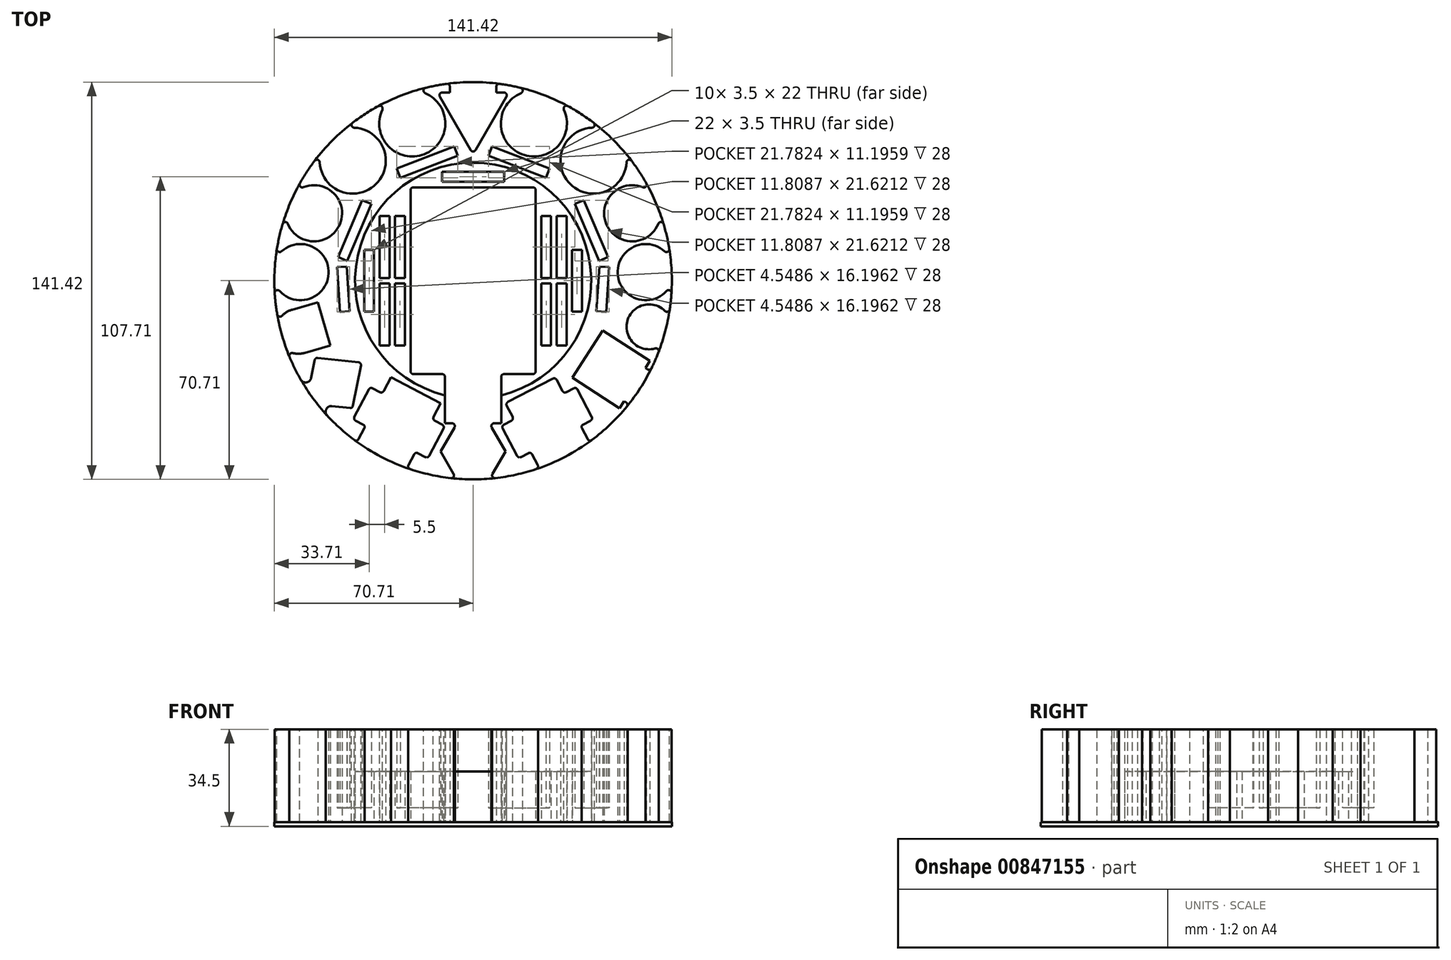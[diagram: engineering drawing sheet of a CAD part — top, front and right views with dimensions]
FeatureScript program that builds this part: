
annotation { "Feature Type Name" : "Feature", "Feature Type Description" : "" }
export const myFeature = defineFeature(function(context is Context, id is Id, definition is map)
    precondition{}
    {
        {
            var Q0;
            Q0=qCreatedBy(makeId("Top.planeOp"),FACE);
            var sketch = newSketch(context, id + "F0", { "sketchPlane" : qUnion([Q0])});
            skLineSegment(sketch, "E0.bottom", {"start": v(-22.25, 33.25) * mm, "end": v(22.25, 33.25) * mm});
            skLineSegment(sketch, "E0.top", {"start": v(-22.25, -33.25) * mm, "end": v(22.25, -33.25) * mm});
            skLineSegment(sketch, "E0.left", {"start": v(-22.25, 33.25) * mm, "end": v(-22.25, -33.25) * mm});
            skLineSegment(sketch, "E0.right", {"start": v(22.25, 33.25) * mm, "end": v(22.25, -33.25) * mm});
            skPoint(sketch, "E0.middle", {"position": v(0, 0) * mm});
            skCircle(sketch, "E1", {"center": v(0, 0) * mm, "radius": 42 * mm});
            skCircle(sketch, "E2", {"center": v(0, 0) * mm, "radius": 70.71 * mm});
            skPoint(sketch, "E3.middle", {"position": v(0, 57) * mm});
            skLineSegment(sketch, "E4.bottom", {"start": v(-10, -33.25) * mm, "end": v(10, -33.25) * mm});
            skLineSegment(sketch, "E4.top", {"start": v(-10, -50.75) * mm, "end": v(10, -50.75) * mm});
            skLineSegment(sketch, "E4.left", {"start": v(-10, -33.25) * mm, "end": v(-10, -50.75) * mm});
            skLineSegment(sketch, "E4.right", {"start": v(10, -33.25) * mm, "end": v(10, -50.75) * mm});
            skPoint(sketch, "E4.middle", {"position": v(0, -42) * mm});
            skCircle(sketch, "E5", {"center": v(0, 0) * mm, "radius": 60 * mm, "construction": true});
            skCircle(sketch, "E6", {"center": v(21.63, 55.97) * mm, "radius": 11.75 * mm});
            skCircle(sketch, "E7", {"center": v(0, 0) * mm, "radius": 61.5 * mm, "construction": true});
            skCircle(sketch, "E8", {"center": v(56.62, 24) * mm, "radius": 10 * mm});
            skCircle(sketch, "E9", {"center": v(0, 0) * mm, "radius": 60.5 * mm, "construction": true});
            skCircle(sketch, "E10", {"center": v(42.84, 42.72) * mm, "radius": 11.75 * mm});
            skCircle(sketch, "E11", {"center": v(61.42, 3.05) * mm, "radius": 10 * mm});
            skCircle(sketch, "E12", {"center": v(0, 0) * mm, "radius": 74 * mm, "construction": true});
            skCircle(sketch, "E13", {"center": v(0, 0) * mm, "radius": 59 * mm, "construction": true});
            skCircle(sketch, "E14.MirrorC", {"center": v(-21.63, 55.97) * mm, "radius": 11.75 * mm});
            skCircle(sketch, "E15.MirrorC", {"center": v(-42.84, 42.72) * mm, "radius": 11.75 * mm});
            skCircle(sketch, "E16.MirrorC", {"center": v(-56.62, 24) * mm, "radius": 10 * mm});
            skCircle(sketch, "E17.MirrorC", {"center": v(-61.42, 3.05) * mm, "radius": 10 * mm});
            skLineSegment(sketch, "E18.bottom", {"start": v(-16.1, -63.23) * mm, "end": v(-42.69, -49.35) * mm});
            skLineSegment(sketch, "E18.top", {"start": v(-10.08, -51.7) * mm, "end": v(-36.67, -37.82) * mm});
            skLineSegment(sketch, "E18.left", {"start": v(-16.1, -63.23) * mm, "end": v(-10.08, -51.7) * mm});
            skLineSegment(sketch, "E18.right", {"start": v(-42.69, -49.35) * mm, "end": v(-36.67, -37.82) * mm});
            skPoint(sketch, "E18.middle", {"position": v(-26.38, -50.53) * mm});
            skLineSegment(sketch, "E19.bottom", {"start": v(-11.5, -43.63) * mm, "end": v(-29.23, -34.38) * mm});
            skLineSegment(sketch, "E19.top", {"start": v(-23.53, -66.68) * mm, "end": v(-41.26, -57.42) * mm});
            skLineSegment(sketch, "E19.left", {"start": v(-11.5, -43.63) * mm, "end": v(-23.53, -66.68) * mm});
            skLineSegment(sketch, "E19.right", {"start": v(-29.23, -34.38) * mm, "end": v(-41.26, -57.42) * mm});
            skLineSegment(sketch, "E20.MirrorCS", {"start": v(11.5, -43.63) * mm, "end": v(29.23, -34.38) * mm});
            skLineSegment(sketch, "E21.MirrorCS", {"start": v(10.08, -51.7) * mm, "end": v(36.67, -37.82) * mm});
            skLineSegment(sketch, "E22.MirrorCS", {"start": v(29.23, -34.38) * mm, "end": v(41.26, -57.42) * mm});
            skLineSegment(sketch, "E23.MirrorCS", {"start": v(42.69, -49.35) * mm, "end": v(36.67, -37.82) * mm});
            skLineSegment(sketch, "E24.MirrorCS", {"start": v(16.1, -63.23) * mm, "end": v(10.08, -51.7) * mm});
            skLineSegment(sketch, "E25.MirrorCS", {"start": v(11.5, -43.63) * mm, "end": v(23.53, -66.68) * mm});
            skLineSegment(sketch, "E26.MirrorCS", {"start": v(23.53, -66.68) * mm, "end": v(41.26, -57.42) * mm});
            skLineSegment(sketch, "E27.MirrorCS", {"start": v(16.1, -63.23) * mm, "end": v(42.69, -49.35) * mm});
            skLineSegment(sketch, "E28", {"start": v(-24.25, 29.08) * mm, "end": v(-24.25, -29.92) * mm, "construction": true});
            skCircle(sketch, "E29", {"center": v(0, 0) * mm, "radius": 40 * mm, "construction": true});
            skLineSegment(sketch, "E30", {"start": v(-46.76, 1) * mm, "end": v(-10.29, 1) * mm, "construction": true});
            skLineSegment(sketch, "E31.bottom", {"start": v(-24.25, 1) * mm, "end": v(-27.75, 1) * mm});
            skLineSegment(sketch, "E31.top", {"start": v(-24.25, 23) * mm, "end": v(-27.75, 23) * mm});
            skLineSegment(sketch, "E31.left", {"start": v(-24.25, 1) * mm, "end": v(-24.25, 23) * mm});
            skLineSegment(sketch, "E31.right", {"start": v(-27.75, 1) * mm, "end": v(-27.75, 23) * mm});
            skLineSegment(sketch, "E32.bottom", {"start": v(-29.75, 1) * mm, "end": v(-33.25, 1) * mm});
            skLineSegment(sketch, "E32.top", {"start": v(-29.75, 23) * mm, "end": v(-33.25, 23) * mm});
            skLineSegment(sketch, "E32.left", {"start": v(-29.75, 1) * mm, "end": v(-29.75, 23) * mm});
            skLineSegment(sketch, "E32.right", {"start": v(-33.25, 1) * mm, "end": v(-33.25, 23) * mm});
            skLineSegment(sketch, "E33.bottom", {"start": v(-35.25, 11) * mm, "end": v(-38.75, 11) * mm});
            skLineSegment(sketch, "E33.top", {"start": v(-35.25, -11) * mm, "end": v(-38.75, -11) * mm});
            skLineSegment(sketch, "E33.left", {"start": v(-35.25, 11) * mm, "end": v(-35.25, -11) * mm});
            skLineSegment(sketch, "E33.right", {"start": v(-38.75, 11) * mm, "end": v(-38.75, -11) * mm});
            skPoint(sketch, "E33.middle", {"position": v(-37, 0) * mm});
            skLineSegment(sketch, "E34.MirrorCS", {"start": v(-29.75, -1) * mm, "end": v(-29.75, -23) * mm});
            skLineSegment(sketch, "E35.MirrorCS", {"start": v(-27.75, -1) * mm, "end": v(-27.75, -23) * mm});
            skLineSegment(sketch, "E36.MirrorCS", {"start": v(-29.75, -1) * mm, "end": v(-33.25, -1) * mm});
            skLineSegment(sketch, "E37.MirrorCS", {"start": v(-24.25, -1) * mm, "end": v(-27.75, -1) * mm});
            skLineSegment(sketch, "E38.MirrorCS", {"start": v(-24.25, -23) * mm, "end": v(-27.75, -23) * mm});
            skLineSegment(sketch, "E39.MirrorCS", {"start": v(-29.75, -23) * mm, "end": v(-33.25, -23) * mm});
            skLineSegment(sketch, "E40.MirrorCS", {"start": v(-33.25, -1) * mm, "end": v(-33.25, -23) * mm});
            skLineSegment(sketch, "E41.MirrorCS", {"start": v(-24.25, -1) * mm, "end": v(-24.25, -23) * mm});
            skLineSegment(sketch, "E42.MirrorCS", {"start": v(24.25, -1) * mm, "end": v(24.25, -23) * mm});
            skLineSegment(sketch, "E43.MirrorCS", {"start": v(24.25, 1) * mm, "end": v(24.25, 23) * mm});
            skLineSegment(sketch, "E44.MirrorCS", {"start": v(29.75, 1) * mm, "end": v(33.25, 1) * mm});
            skLineSegment(sketch, "E45.MirrorCS", {"start": v(29.75, -1) * mm, "end": v(33.25, -1) * mm});
            skLineSegment(sketch, "E46.MirrorCS", {"start": v(24.25, 1) * mm, "end": v(27.75, 1) * mm});
            skLineSegment(sketch, "E47.MirrorCS", {"start": v(24.25, -1) * mm, "end": v(27.75, -1) * mm});
            skLineSegment(sketch, "E48.MirrorCS", {"start": v(24.25, 29.08) * mm, "end": v(24.25, -29.92) * mm, "construction": true});
            skLineSegment(sketch, "E49.MirrorCS", {"start": v(24.25, -23) * mm, "end": v(27.75, -23) * mm});
            skLineSegment(sketch, "E50.MirrorCS", {"start": v(35.25, 11) * mm, "end": v(38.75, 11) * mm});
            skLineSegment(sketch, "E51.MirrorCS", {"start": v(29.75, -1) * mm, "end": v(29.75, -23) * mm});
            skLineSegment(sketch, "E52.MirrorCS", {"start": v(35.25, -11) * mm, "end": v(38.75, -11) * mm});
            skLineSegment(sketch, "E53.MirrorCS", {"start": v(29.75, 23) * mm, "end": v(33.25, 23) * mm});
            skLineSegment(sketch, "E54.MirrorCS", {"start": v(38.75, 11) * mm, "end": v(38.75, -11) * mm});
            skLineSegment(sketch, "E55.MirrorCS", {"start": v(24.25, 23) * mm, "end": v(27.75, 23) * mm});
            skPoint(sketch, "E56.MirrorP", {"position": v(37, 0) * mm});
            skLineSegment(sketch, "E57.MirrorCS", {"start": v(46.76, 1) * mm, "end": v(10.29, 1) * mm, "construction": true});
            skLineSegment(sketch, "E58.MirrorCS", {"start": v(27.75, -1) * mm, "end": v(27.75, -23) * mm});
            skLineSegment(sketch, "E59.MirrorCS", {"start": v(33.25, 1) * mm, "end": v(33.25, 23) * mm});
            skLineSegment(sketch, "E60.MirrorCS", {"start": v(35.25, 11) * mm, "end": v(35.25, -11) * mm});
            skLineSegment(sketch, "E61.MirrorCS", {"start": v(29.75, -23) * mm, "end": v(33.25, -23) * mm});
            skLineSegment(sketch, "E62.MirrorCS", {"start": v(29.75, 1) * mm, "end": v(29.75, 23) * mm});
            skLineSegment(sketch, "E63.MirrorCS", {"start": v(27.75, 1) * mm, "end": v(27.75, 23) * mm});
            skLineSegment(sketch, "E64.MirrorCS", {"start": v(33.25, -1) * mm, "end": v(33.25, -23) * mm});
            skLineSegment(sketch, "E65.bottom", {"start": v(11, 35.25) * mm, "end": v(-11, 35.25) * mm});
            skLineSegment(sketch, "E65.top", {"start": v(11, 38.75) * mm, "end": v(-11, 38.75) * mm});
            skLineSegment(sketch, "E65.left", {"start": v(11, 35.25) * mm, "end": v(11, 38.75) * mm});
            skLineSegment(sketch, "E65.right", {"start": v(-11, 35.25) * mm, "end": v(-11, 38.75) * mm});
            skPoint(sketch, "E65.middle", {"position": v(0, 37) * mm});
            skLineSegment(sketch, "E66", {"start": v(0, 0) * mm, "end": v(-21.63, 55.97) * mm, "construction": true});
            skLineSegment(sketch, "E67.bottom", {"start": v(-6.68, 47.8) * mm, "end": v(-27.2, 39.87) * mm});
            skLineSegment(sketch, "E67.top", {"start": v(-5.42, 44.54) * mm, "end": v(-25.94, 36.6) * mm});
            skLineSegment(sketch, "E67.left", {"start": v(-6.68, 47.8) * mm, "end": v(-5.42, 44.54) * mm});
            skLineSegment(sketch, "E67.right", {"start": v(-27.2, 39.87) * mm, "end": v(-25.94, 36.6) * mm});
            skPoint(sketch, "E67.middle", {"position": v(-16.31, 42.2) * mm});
            skLineSegment(sketch, "E68", {"start": v(-56.62, 24) * mm, "end": v(0, 0) * mm, "construction": true});
            skLineSegment(sketch, "E69.bottom", {"start": v(-36.22, 27.3) * mm, "end": v(-39.44, 28.67) * mm});
            skLineSegment(sketch, "E69.top", {"start": v(-44.8, 7.04) * mm, "end": v(-48.03, 8.41) * mm});
            skLineSegment(sketch, "E69.left", {"start": v(-36.22, 27.3) * mm, "end": v(-44.8, 7.04) * mm});
            skLineSegment(sketch, "E69.right", {"start": v(-39.44, 28.67) * mm, "end": v(-48.03, 8.41) * mm});
            skPoint(sketch, "E69.middle", {"position": v(-42.12, 17.86) * mm});
            skLineSegment(sketch, "E70.MirrorCS", {"start": v(27.2, 39.87) * mm, "end": v(25.94, 36.6) * mm});
            skLineSegment(sketch, "E71.MirrorCS", {"start": v(6.68, 47.8) * mm, "end": v(27.2, 39.87) * mm});
            skLineSegment(sketch, "E72.MirrorCS", {"start": v(5.42, 44.54) * mm, "end": v(25.94, 36.6) * mm});
            skLineSegment(sketch, "E73.MirrorCS", {"start": v(6.68, 47.8) * mm, "end": v(5.42, 44.54) * mm});
            skLineSegment(sketch, "E74.MirrorCS", {"start": v(39.44, 28.67) * mm, "end": v(48.03, 8.41) * mm});
            skLineSegment(sketch, "E75.MirrorCS", {"start": v(36.22, 27.3) * mm, "end": v(44.8, 7.04) * mm});
            skLineSegment(sketch, "E76.MirrorCS", {"start": v(36.22, 27.3) * mm, "end": v(39.44, 28.67) * mm});
            skLineSegment(sketch, "E77.MirrorCS", {"start": v(44.8, 7.04) * mm, "end": v(48.03, 8.41) * mm});
            skLineSegment(sketch, "E78", {"start": v(0, 0) * mm, "end": v(-52.23, -3.46) * mm, "construction": true});
            skLineSegment(sketch, "E79.bottom", {"start": v(-48.42, 4.81) * mm, "end": v(-44.93, 5.04) * mm});
            skLineSegment(sketch, "E79.top", {"start": v(-47.37, -11.15) * mm, "end": v(-43.87, -10.92) * mm});
            skLineSegment(sketch, "E79.left", {"start": v(-48.42, 4.81) * mm, "end": v(-47.37, -11.15) * mm});
            skLineSegment(sketch, "E79.right", {"start": v(-44.93, 5.04) * mm, "end": v(-43.87, -10.92) * mm});
            skPoint(sketch, "E79.middle", {"position": v(-46.15, -3.05) * mm});
            skLineSegment(sketch, "E80.MirrorCS", {"start": v(48.42, 4.81) * mm, "end": v(44.93, 5.04) * mm});
            skLineSegment(sketch, "E81.MirrorCS", {"start": v(47.37, -11.15) * mm, "end": v(43.87, -10.92) * mm});
            skLineSegment(sketch, "E82.MirrorCS", {"start": v(48.42, 4.81) * mm, "end": v(47.37, -11.15) * mm});
            skLineSegment(sketch, "E83.MirrorCS", {"start": v(44.93, 5.04) * mm, "end": v(43.87, -10.92) * mm});
            skPoint(sketch, "E84.MirrorP", {"position": v(46.15, -3.05) * mm});
            skCircle(sketch, "E85.cCircle", {"center": v(0, -60.75) * mm, "radius": 10 * mm, "construction": true});
            skLineSegment(sketch, "E85.0", {"start": v(-5.77, -50.75) * mm, "end": v(5.77, -50.75) * mm});
            skLineSegment(sketch, "E85.1", {"start": v(5.77, -50.75) * mm, "end": v(11.55, -60.75) * mm});
            skLineSegment(sketch, "E85.2", {"start": v(11.55, -60.75) * mm, "end": v(5.77, -70.75) * mm});
            skLineSegment(sketch, "E85.3", {"start": v(5.77, -70.75) * mm, "end": v(-5.77, -70.75) * mm});
            skLineSegment(sketch, "E85.4", {"start": v(-5.77, -70.75) * mm, "end": v(-11.55, -60.75) * mm});
            skLineSegment(sketch, "E85.5", {"start": v(-11.55, -60.75) * mm, "end": v(-5.77, -50.75) * mm});
            skPoint(sketch, "E85.0.midPoint", {"position": v(0, -50.75) * mm});
            skLineSegment(sketch, "E86.MirrorCS", {"start": v(-13.28, 68) * mm, "end": v(13.28, 68) * mm});
            skLineSegment(sketch, "E87", {"start": v(13.28, 68) * mm, "end": v(0, 45) * mm});
            skLineSegment(sketch, "E88", {"start": v(0, 45) * mm, "end": v(-13.28, 68) * mm});
            skLineSegment(sketch, "E89", {"start": v(-8.28, 70.22) * mm, "end": v(-8.28, 68) * mm});
            skLineSegment(sketch, "E90.MirrorCS", {"start": v(8.28, 70.22) * mm, "end": v(8.28, 68) * mm});
            skCircle(sketch, "E91", {"center": v(-62.16, -17.99) * mm, "radius": 8 * mm});
            skLineSegment(sketch, "E92", {"start": v(-59.94, -25.67) * mm, "end": v(-50.81, -23.03) * mm});
            skLineSegment(sketch, "E93", {"start": v(-50.81, -23.03) * mm, "end": v(-55.26, -7.66) * mm});
            skLineSegment(sketch, "E94", {"start": v(-55.26, -7.66) * mm, "end": v(-64.38, -10.3) * mm});
            skLineSegment(sketch, "E95.bottom", {"start": v(62.92, -28.54) * mm, "end": v(46.1, -17.73) * mm});
            skLineSegment(sketch, "E95.top", {"start": v(52.1, -45.37) * mm, "end": v(35.28, -34.56) * mm});
            skLineSegment(sketch, "E95.left", {"start": v(62.92, -28.54) * mm, "end": v(52.1, -45.37) * mm});
            skLineSegment(sketch, "E95.right", {"start": v(46.1, -17.73) * mm, "end": v(35.28, -34.56) * mm});
            skPoint(sketch, "E95.middle", {"position": v(49.1, -31.55) * mm});
            skLineSegment(sketch, "E96", {"start": v(49.1, -31.55) * mm, "end": v(0, 0) * mm, "construction": true});
            skLineSegment(sketch, "E97", {"start": v(61.3, -31.06) * mm, "end": v(62.98, -32.14) * mm});
            skLineSegment(sketch, "E98.MirrorCS", {"start": v(53.73, -42.84) * mm, "end": v(55.41, -43.92) * mm});
            skLineSegment(sketch, "E99", {"start": v(-59.4, -43.66) * mm, "end": v(-56.19, -27.37) * mm});
            skLineSegment(sketch, "E100", {"start": v(-56.19, -27.37) * mm, "end": v(-39.68, -29.16) * mm});
            skLineSegment(sketch, "E101", {"start": v(-39.68, -29.16) * mm, "end": v(-42.9, -45.45) * mm});
            skLineSegment(sketch, "E102", {"start": v(-42.9, -45.45) * mm, "end": v(-59.4, -43.66) * mm});
            skCircle(sketch, "E103", {"center": v(0, 0) * mm, "radius": 62.5 * mm, "construction": true});
            skLineSegment(sketch, "E104", {"start": v(-69.25, -14.29) * mm, "end": v(-66.18, -24.9) * mm, "construction": true});
            skCircle(sketch, "E105.MirrorC", {"center": v(62.6, -16.42) * mm, "radius": 8 * mm});
            skLineSegment(sketch, "E106", {"start": v(-12.7, 67) * mm, "end": v(12.7, 67) * mm});
            skLineSegment(sketch, "E107", {"start": v(-8.28, 68) * mm, "end": v(-8.28, 67) * mm});
            skLineSegment(sketch, "E108", {"start": v(8.28, 68) * mm, "end": v(8.28, 67) * mm});
            skLineSegment(sketch, "E109.bottom", {"start": v(28.25, 38.25) * mm, "end": v(-28.25, 38.25) * mm, "construction": true});
            skLineSegment(sketch, "E109.top", {"start": v(28.25, -38.25) * mm, "end": v(-28.25, -38.25) * mm, "construction": true});
            skLineSegment(sketch, "E109.left", {"start": v(28.25, 38.25) * mm, "end": v(28.25, -38.25) * mm, "construction": true});
            skLineSegment(sketch, "E109.right", {"start": v(-28.25, 38.25) * mm, "end": v(-28.25, -38.25) * mm, "construction": true});
            skSolve(sketch);
        }
        {
            var Q0;
            Q0=makeQuery(id+"F0.imprint","IMPRINT",FACE,{"disambiguationData":[TD([[makeQuery(id+"F0.imprint","IMPRINT",EDGE,{"derivedFrom":sQuery(id+"F0.wireOp",EDGE,"E0.bottom")}),1.0]])]});
            extrude(context, id + "F1", {"entities" : qUnion([Q0]), "depth" : 18 * mm, "offsetDistance" : 25 * mm});
        }
        {
            var Q0;
            Q0=makeQuery(id+"F1.opExtrude","SWEPT_EDGE",EDGE,{"disambiguationData":[OSD([sQuery(id+"F0.wireOp",EDGE,"E0.bottom"),sQuery(id+"F0.wireOp",EDGE,"E0.left")])]});
            var Q1;
            Q1=makeQuery(id+"F1.opExtrude","SWEPT_EDGE",EDGE,{"disambiguationData":[OSD([sQuery(id+"F0.wireOp",EDGE,"E0.bottom"),sQuery(id+"F0.wireOp",EDGE,"E0.right")])]});
            var Q2;
            Q2=makeQuery(id+"F1.opExtrude","SWEPT_EDGE",EDGE,{"disambiguationData":[OSD([sQuery(id+"F0.wireOp",EDGE,"E0.top"),sQuery(id+"F0.wireOp",EDGE,"E0.left")])]});
            var Q3;
            Q3=makeQuery(id+"F1.opExtrude","SWEPT_EDGE",EDGE,{"disambiguationData":[OSD([sQuery(id+"F0.wireOp",EDGE,"E0.top"),sQuery(id+"F0.wireOp",EDGE,"E4.bottom"),sQuery(id+"F0.wireOp",EDGE,"E4.left")])]});
            var Q4;
            Q4=makeQuery(id+"F1.opExtrude","SWEPT_EDGE",EDGE,{"disambiguationData":[OSD([sQuery(id+"F0.wireOp",EDGE,"E0.top"),sQuery(id+"F0.wireOp",EDGE,"E4.bottom"),sQuery(id+"F0.wireOp",EDGE,"E4.right")])]});
            var Q5;
            Q5=makeQuery(id+"F1.opExtrude","SWEPT_EDGE",EDGE,{"disambiguationData":[OSD([sQuery(id+"F0.wireOp",EDGE,"E0.top"),sQuery(id+"F0.wireOp",EDGE,"E0.right")])]});
            fillet(context, id + "F2", {"entities" : qUnion([Q0, Q1, Q2, Q3, Q4, Q5]), "radius" : 1 * mm, "tangentPropagation" : true, "allowEdgeOverflow" : false});
        }
        {
            var Q0;
            {var subQ69=sQuery(id+"F0.wireOp",EDGE,"E4.top");Q0=makeQuery(id+"F0.imprint","IMPRINT",FACE,{"disambiguationData":[TD([[makeQuery(id+"F0.imprint","IMPRINT",EDGE,{"derivedFrom":subQ69}),-1.0]])]});}
            var Q1;
            {var subQ3=sQuery(id+"F0.wireOp",EDGE,"E107");Q1=makeQuery(id+"F0.imprint","IMPRINT",FACE,{"disambiguationData":[TD([[makeQuery(id+"F0.imprint","IMPRINT",EDGE,{"derivedFrom":subQ3}),-1.0]])]});}
            var Q2;
            {var subQ3=sQuery(id+"F0.wireOp",EDGE,"E108");Q2=makeQuery(id+"F0.imprint","IMPRINT",FACE,{"disambiguationData":[TD([[makeQuery(id+"F0.imprint","IMPRINT",EDGE,{"derivedFrom":subQ3}),1.0]])]});}
            extrude(context, id + "F3", {"entities" : qUnion([Q0, Q1, Q2]), "depth" : 33 * mm, "offsetDistance" : 25 * mm});
        }
        {
            var Q0;
            Q0=makeQuery(id+"F3.opExtrude","SWEPT_EDGE",EDGE,{"disambiguationData":[OSD([sQuery(id+"F0.wireOp",EDGE,"E2"),sQuery(id+"F0.wireOp",EDGE,"E89")])]});
            var Q1;
            Q1=makeQuery(id+"F3.opExtrude","SWEPT_EDGE",EDGE,{"disambiguationData":[OSD([sQuery(id+"F0.wireOp",EDGE,"E2"),sQuery(id+"F0.wireOp",EDGE,"E90.MirrorCS")])]});
            var Q2;
            Q2=makeQuery(id+"F3.opExtrude","SWEPT_EDGE",EDGE,{"disambiguationData":[OSD([sQuery(id+"F0.wireOp",EDGE,"E2"),sQuery(id+"F0.wireOp",EDGE,"E97")])]});
            var Q3;
            Q3=makeQuery(id+"F3.opExtrude","SWEPT_EDGE",EDGE,{"disambiguationData":[OSD([sQuery(id+"F0.wireOp",EDGE,"E2"),sQuery(id+"F0.wireOp",EDGE,"E98.MirrorCS")])]});
            var Q4;
            {var subQ0=sQuery(id+"F0.wireOp",EDGE,"E8");var subQ1=sQuery(id+"F0.wireOp",EDGE,"E2");Q4=makeQuery(id+"F3.opExtrude","SWEPT_EDGE",EDGE,{"disambiguationData":[OSD([subQ1,subQ0]),TDD([makeQuery(id+"F0.imprint","INTERSECT",VERTEX,{"disambiguationData":[OD(0.0)],"derivedFrom":[subQ1,subQ0]})])]});}
            var Q5;
            {var subQ0=sQuery(id+"F0.wireOp",EDGE,"E11");var subQ1=sQuery(id+"F0.wireOp",EDGE,"E2");Q5=makeQuery(id+"F3.opExtrude","SWEPT_EDGE",EDGE,{"disambiguationData":[OSD([subQ1,subQ0]),TDD([makeQuery(id+"F0.imprint","INTERSECT",VERTEX,{"disambiguationData":[OD(0.0)],"derivedFrom":[subQ1,subQ0]})])]});}
            var Q6;
            {var subQ0=sQuery(id+"F0.wireOp",EDGE,"E8");var subQ1=sQuery(id+"F0.wireOp",EDGE,"E2");Q6=makeQuery(id+"F3.opExtrude","SWEPT_EDGE",EDGE,{"disambiguationData":[OSD([subQ1,subQ0]),TDD([makeQuery(id+"F0.imprint","INTERSECT",VERTEX,{"disambiguationData":[OD(1.0)],"derivedFrom":[subQ1,subQ0]})])]});}
            var Q7;
            {var subQ0=sQuery(id+"F0.wireOp",EDGE,"E10");var subQ1=sQuery(id+"F0.wireOp",EDGE,"E2");Q7=makeQuery(id+"F3.opExtrude","SWEPT_EDGE",EDGE,{"disambiguationData":[OSD([subQ1,subQ0]),TDD([makeQuery(id+"F0.imprint","INTERSECT",VERTEX,{"disambiguationData":[OD(0.0)],"derivedFrom":[subQ1,subQ0]})])]});}
            var Q8;
            {var subQ0=sQuery(id+"F0.wireOp",EDGE,"E10");var subQ1=sQuery(id+"F0.wireOp",EDGE,"E2");Q8=makeQuery(id+"F3.opExtrude","SWEPT_EDGE",EDGE,{"disambiguationData":[OSD([subQ1,subQ0]),TDD([makeQuery(id+"F0.imprint","INTERSECT",VERTEX,{"disambiguationData":[OD(1.0)],"derivedFrom":[subQ1,subQ0]})])]});}
            var Q9;
            {var subQ0=sQuery(id+"F0.wireOp",EDGE,"E6");var subQ1=sQuery(id+"F0.wireOp",EDGE,"E2");Q9=makeQuery(id+"F3.opExtrude","SWEPT_EDGE",EDGE,{"disambiguationData":[OSD([subQ1,subQ0]),TDD([makeQuery(id+"F0.imprint","INTERSECT",VERTEX,{"disambiguationData":[OD(0.0)],"derivedFrom":[subQ1,subQ0]})])]});}
            var Q10;
            {var subQ0=sQuery(id+"F0.wireOp",EDGE,"E6");var subQ1=sQuery(id+"F0.wireOp",EDGE,"E2");Q10=makeQuery(id+"F3.opExtrude","SWEPT_EDGE",EDGE,{"disambiguationData":[OSD([subQ1,subQ0]),TDD([makeQuery(id+"F0.imprint","INTERSECT",VERTEX,{"disambiguationData":[OD(1.0)],"derivedFrom":[subQ1,subQ0]})])]});}
            var Q11;
            {var subQ0=sQuery(id+"F0.wireOp",EDGE,"E14.MirrorC");var subQ1=sQuery(id+"F0.wireOp",EDGE,"E2");Q11=makeQuery(id+"F3.opExtrude","SWEPT_EDGE",EDGE,{"disambiguationData":[OSD([subQ1,subQ0]),TDD([makeQuery(id+"F0.imprint","INTERSECT",VERTEX,{"disambiguationData":[OD(0.0)],"derivedFrom":[subQ1,subQ0]})])]});}
            var Q12;
            {var subQ0=sQuery(id+"F0.wireOp",EDGE,"E14.MirrorC");var subQ1=sQuery(id+"F0.wireOp",EDGE,"E2");Q12=makeQuery(id+"F3.opExtrude","SWEPT_EDGE",EDGE,{"disambiguationData":[OSD([subQ1,subQ0]),TDD([makeQuery(id+"F0.imprint","INTERSECT",VERTEX,{"disambiguationData":[OD(1.0)],"derivedFrom":[subQ1,subQ0]})])]});}
            var Q13;
            {var subQ0=sQuery(id+"F0.wireOp",EDGE,"E15.MirrorC");var subQ1=sQuery(id+"F0.wireOp",EDGE,"E2");Q13=makeQuery(id+"F3.opExtrude","SWEPT_EDGE",EDGE,{"disambiguationData":[OSD([subQ1,subQ0]),TDD([makeQuery(id+"F0.imprint","INTERSECT",VERTEX,{"disambiguationData":[OD(0.0)],"derivedFrom":[subQ1,subQ0]})])]});}
            var Q14;
            {var subQ0=sQuery(id+"F0.wireOp",EDGE,"E15.MirrorC");var subQ1=sQuery(id+"F0.wireOp",EDGE,"E2");Q14=makeQuery(id+"F3.opExtrude","SWEPT_EDGE",EDGE,{"disambiguationData":[OSD([subQ1,subQ0]),TDD([makeQuery(id+"F0.imprint","INTERSECT",VERTEX,{"disambiguationData":[OD(1.0)],"derivedFrom":[subQ1,subQ0]})])]});}
            var Q15;
            {var subQ0=sQuery(id+"F0.wireOp",EDGE,"E16.MirrorC");var subQ1=sQuery(id+"F0.wireOp",EDGE,"E2");Q15=makeQuery(id+"F3.opExtrude","SWEPT_EDGE",EDGE,{"disambiguationData":[OSD([subQ1,subQ0]),TDD([makeQuery(id+"F0.imprint","INTERSECT",VERTEX,{"disambiguationData":[OD(0.0)],"derivedFrom":[subQ1,subQ0]})])]});}
            var Q16;
            {var subQ0=sQuery(id+"F0.wireOp",EDGE,"E16.MirrorC");var subQ1=sQuery(id+"F0.wireOp",EDGE,"E2");Q16=makeQuery(id+"F3.opExtrude","SWEPT_EDGE",EDGE,{"disambiguationData":[OSD([subQ1,subQ0]),TDD([makeQuery(id+"F0.imprint","INTERSECT",VERTEX,{"disambiguationData":[OD(1.0)],"derivedFrom":[subQ1,subQ0]})])]});}
            var Q17;
            {var subQ0=sQuery(id+"F0.wireOp",EDGE,"E17.MirrorC");var subQ1=sQuery(id+"F0.wireOp",EDGE,"E2");Q17=makeQuery(id+"F3.opExtrude","SWEPT_EDGE",EDGE,{"disambiguationData":[OSD([subQ1,subQ0]),TDD([makeQuery(id+"F0.imprint","INTERSECT",VERTEX,{"disambiguationData":[OD(0.0)],"derivedFrom":[subQ1,subQ0]})])]});}
            var Q18;
            {var subQ0=sQuery(id+"F0.wireOp",EDGE,"E17.MirrorC");var subQ1=sQuery(id+"F0.wireOp",EDGE,"E2");Q18=makeQuery(id+"F3.opExtrude","SWEPT_EDGE",EDGE,{"disambiguationData":[OSD([subQ1,subQ0]),TDD([makeQuery(id+"F0.imprint","INTERSECT",VERTEX,{"disambiguationData":[OD(1.0)],"derivedFrom":[subQ1,subQ0]})])]});}
            var Q19;
            {var subQ0=sQuery(id+"F0.wireOp",EDGE,"E91");var subQ1=sQuery(id+"F0.wireOp",EDGE,"E2");Q19=makeQuery(id+"F3.opExtrude","SWEPT_EDGE",EDGE,{"disambiguationData":[OSD([subQ1,subQ0]),TDD([makeQuery(id+"F0.imprint","INTERSECT",VERTEX,{"disambiguationData":[OD(0.0)],"derivedFrom":[subQ1,subQ0]})])]});}
            var Q20;
            {var subQ0=sQuery(id+"F0.wireOp",EDGE,"E91");var subQ1=sQuery(id+"F0.wireOp",EDGE,"E2");Q20=makeQuery(id+"F3.opExtrude","SWEPT_EDGE",EDGE,{"disambiguationData":[OSD([subQ1,subQ0]),TDD([makeQuery(id+"F0.imprint","INTERSECT",VERTEX,{"disambiguationData":[OD(1.0)],"derivedFrom":[subQ1,subQ0]})])]});}
            var Q21;
            Q21=makeQuery(id+"F3.opExtrude","SWEPT_EDGE",EDGE,{"disambiguationData":[OSD([sQuery(id+"F0.wireOp",EDGE,"E2"),sQuery(id+"F0.wireOp",EDGE,"E85.4")])]});
            var Q22;
            Q22=makeQuery(id+"F3.opExtrude","SWEPT_EDGE",EDGE,{"disambiguationData":[OSD([sQuery(id+"F0.wireOp",EDGE,"E2"),sQuery(id+"F0.wireOp",EDGE,"E85.2")])]});
            var Q23;
            {var subQ0=sQuery(id+"F0.wireOp",EDGE,"E105.MirrorC");var subQ1=sQuery(id+"F0.wireOp",EDGE,"E2");Q23=makeQuery(id+"F3.opExtrude","SWEPT_EDGE",EDGE,{"disambiguationData":[OSD([subQ1,subQ0]),TDD([makeQuery(id+"F0.imprint","INTERSECT",VERTEX,{"disambiguationData":[OD(0.0)],"derivedFrom":[subQ1,subQ0]})])]});}
            var Q24;
            {var subQ0=sQuery(id+"F0.wireOp",EDGE,"E105.MirrorC");var subQ1=sQuery(id+"F0.wireOp",EDGE,"E2");Q24=makeQuery(id+"F3.opExtrude","SWEPT_EDGE",EDGE,{"disambiguationData":[OSD([subQ1,subQ0]),TDD([makeQuery(id+"F0.imprint","INTERSECT",VERTEX,{"disambiguationData":[OD(1.0)],"derivedFrom":[subQ1,subQ0]})])]});}
            var Q25;
            {var subQ0=sQuery(id+"F0.wireOp",EDGE,"E11");var subQ1=sQuery(id+"F0.wireOp",EDGE,"E2");Q25=makeQuery(id+"F3.opExtrude","SWEPT_EDGE",EDGE,{"disambiguationData":[OSD([subQ1,subQ0]),TDD([makeQuery(id+"F0.imprint","INTERSECT",VERTEX,{"disambiguationData":[OD(1.0)],"derivedFrom":[subQ1,subQ0]})])]});}
            var Q26;
            Q26=makeQuery(id+"F3.opExtrude","SWEPT_EDGE",EDGE,{"disambiguationData":[OSD([sQuery(id+"F0.wireOp",EDGE,"E2"),sQuery(id+"F0.wireOp",EDGE,"E19.top"),sQuery(id+"F0.wireOp",EDGE,"E19.left")])]});
            var Q27;
            Q27=makeQuery(id+"F3.opExtrude","SWEPT_EDGE",EDGE,{"disambiguationData":[OSD([sQuery(id+"F0.wireOp",EDGE,"E2"),sQuery(id+"F0.wireOp",EDGE,"E19.top"),sQuery(id+"F0.wireOp",EDGE,"E19.right")])]});
            var Q28;
            Q28=makeQuery(id+"F3.opExtrude","SWEPT_EDGE",EDGE,{"disambiguationData":[OSD([sQuery(id+"F0.wireOp",EDGE,"E2"),sQuery(id+"F0.wireOp",EDGE,"E22.MirrorCS"),sQuery(id+"F0.wireOp",EDGE,"E26.MirrorCS")])]});
            var Q29;
            Q29=makeQuery(id+"F3.opExtrude","SWEPT_EDGE",EDGE,{"disambiguationData":[OSD([sQuery(id+"F0.wireOp",EDGE,"E2"),sQuery(id+"F0.wireOp",EDGE,"E25.MirrorCS"),sQuery(id+"F0.wireOp",EDGE,"E26.MirrorCS")])]});
            var Q30;
            Q30=makeQuery(id+"F3.opExtrude","SWEPT_EDGE",EDGE,{"disambiguationData":[OSD([sQuery(id+"F0.wireOp",EDGE,"E4.top"),sQuery(id+"F0.wireOp",EDGE,"E85.0"),sQuery(id+"F0.wireOp",EDGE,"E85.1")])]});
            var Q31;
            Q31=makeQuery(id+"F3.opExtrude","SWEPT_EDGE",EDGE,{"disambiguationData":[OSD([sQuery(id+"F0.wireOp",EDGE,"E4.top"),sQuery(id+"F0.wireOp",EDGE,"E85.0"),sQuery(id+"F0.wireOp",EDGE,"E85.5")])]});
            var Q32;
            Q32=makeQuery(id+"F3.opExtrude","SWEPT_EDGE",EDGE,{"disambiguationData":[OSD([sQuery(id+"F0.wireOp",EDGE,"E18.top"),sQuery(id+"F0.wireOp",EDGE,"E19.left")])]});
            var Q33;
            Q33=makeQuery(id+"F3.opExtrude","SWEPT_EDGE",EDGE,{"disambiguationData":[OSD([sQuery(id+"F0.wireOp",EDGE,"E18.bottom"),sQuery(id+"F0.wireOp",EDGE,"E19.left")])]});
            var Q34;
            Q34=makeQuery(id+"F3.opExtrude","SWEPT_EDGE",EDGE,{"disambiguationData":[OSD([sQuery(id+"F0.wireOp",EDGE,"E18.bottom"),sQuery(id+"F0.wireOp",EDGE,"E18.left")])]});
            var Q35;
            Q35=makeQuery(id+"F3.opExtrude","SWEPT_EDGE",EDGE,{"disambiguationData":[OSD([sQuery(id+"F0.wireOp",EDGE,"E18.top"),sQuery(id+"F0.wireOp",EDGE,"E18.left")])]});
            var Q36;
            Q36=makeQuery(id+"F3.opExtrude","SWEPT_EDGE",EDGE,{"disambiguationData":[OSD([sQuery(id+"F0.wireOp",EDGE,"E18.top"),sQuery(id+"F0.wireOp",EDGE,"E19.right")])]});
            var Q37;
            Q37=makeQuery(id+"F3.opExtrude","SWEPT_EDGE",EDGE,{"disambiguationData":[OSD([sQuery(id+"F0.wireOp",EDGE,"E18.bottom"),sQuery(id+"F0.wireOp",EDGE,"E19.right")])]});
            var Q38;
            Q38=makeQuery(id+"F3.opExtrude","SWEPT_EDGE",EDGE,{"disambiguationData":[OSD([sQuery(id+"F0.wireOp",EDGE,"E18.top"),sQuery(id+"F0.wireOp",EDGE,"E18.right")])]});
            var Q39;
            Q39=makeQuery(id+"F3.opExtrude","SWEPT_EDGE",EDGE,{"disambiguationData":[OSD([sQuery(id+"F0.wireOp",EDGE,"E18.bottom"),sQuery(id+"F0.wireOp",EDGE,"E18.right")])]});
            var Q40;
            Q40=makeQuery(id+"F3.opExtrude","SWEPT_EDGE",EDGE,{"disambiguationData":[OSD([sQuery(id+"F0.wireOp",EDGE,"E23.MirrorCS"),sQuery(id+"F0.wireOp",EDGE,"E27.MirrorCS")])]});
            var Q41;
            Q41=makeQuery(id+"F3.opExtrude","SWEPT_EDGE",EDGE,{"disambiguationData":[OSD([sQuery(id+"F0.wireOp",EDGE,"E24.MirrorCS"),sQuery(id+"F0.wireOp",EDGE,"E27.MirrorCS")])]});
            var Q42;
            Q42=makeQuery(id+"F3.opExtrude","SWEPT_EDGE",EDGE,{"disambiguationData":[OSD([sQuery(id+"F0.wireOp",EDGE,"E25.MirrorCS"),sQuery(id+"F0.wireOp",EDGE,"E27.MirrorCS")])]});
            var Q43;
            Q43=makeQuery(id+"F3.opExtrude","SWEPT_EDGE",EDGE,{"disambiguationData":[OSD([sQuery(id+"F0.wireOp",EDGE,"E22.MirrorCS"),sQuery(id+"F0.wireOp",EDGE,"E27.MirrorCS")])]});
            var Q44;
            Q44=makeQuery(id+"F3.opExtrude","SWEPT_EDGE",EDGE,{"disambiguationData":[OSD([sQuery(id+"F0.wireOp",EDGE,"E21.MirrorCS"),sQuery(id+"F0.wireOp",EDGE,"E23.MirrorCS")])]});
            var Q45;
            Q45=makeQuery(id+"F3.opExtrude","SWEPT_EDGE",EDGE,{"disambiguationData":[OSD([sQuery(id+"F0.wireOp",EDGE,"E21.MirrorCS"),sQuery(id+"F0.wireOp",EDGE,"E22.MirrorCS")])]});
            var Q46;
            Q46=makeQuery(id+"F3.opExtrude","SWEPT_EDGE",EDGE,{"disambiguationData":[OSD([sQuery(id+"F0.wireOp",EDGE,"E20.MirrorCS"),sQuery(id+"F0.wireOp",EDGE,"E22.MirrorCS")])]});
            var Q47;
            Q47=makeQuery(id+"F3.opExtrude","SWEPT_EDGE",EDGE,{"disambiguationData":[OSD([sQuery(id+"F0.wireOp",EDGE,"E20.MirrorCS"),sQuery(id+"F0.wireOp",EDGE,"E25.MirrorCS")])]});
            var Q48;
            Q48=makeQuery(id+"F3.opExtrude","SWEPT_EDGE",EDGE,{"disambiguationData":[OSD([sQuery(id+"F0.wireOp",EDGE,"E21.MirrorCS"),sQuery(id+"F0.wireOp",EDGE,"E25.MirrorCS")])]});
            var Q49;
            Q49=makeQuery(id+"F3.opExtrude","SWEPT_EDGE",EDGE,{"disambiguationData":[OSD([sQuery(id+"F0.wireOp",EDGE,"E21.MirrorCS"),sQuery(id+"F0.wireOp",EDGE,"E24.MirrorCS")])]});
            var Q50;
            Q50=makeQuery(id+"F3.opExtrude","SWEPT_EDGE",EDGE,{"disambiguationData":[OSD([sQuery(id+"F0.wireOp",EDGE,"E86.MirrorCS"),sQuery(id+"F0.wireOp",EDGE,"E88")])]});
            var Q51;
            Q51=makeQuery(id+"F3.opExtrude","SWEPT_EDGE",EDGE,{"disambiguationData":[OSD([sQuery(id+"F0.wireOp",EDGE,"E86.MirrorCS"),sQuery(id+"F0.wireOp",EDGE,"E87")])]});
            var Q52;
            Q52=makeQuery(id+"F3.opExtrude","SWEPT_EDGE",EDGE,{"disambiguationData":[OSD([sQuery(id+"F0.wireOp",EDGE,"E87"),sQuery(id+"F0.wireOp",EDGE,"E88")])]});
            var Q53;
            Q53=makeQuery(id+"F3.opExtrude","SWEPT_EDGE",EDGE,{"disambiguationData":[OSD([sQuery(id+"F0.wireOp",EDGE,"E99"),sQuery(id+"F0.wireOp",EDGE,"E100")])]});
            var Q54;
            Q54=makeQuery(id+"F3.opExtrude","SWEPT_EDGE",EDGE,{"disambiguationData":[OSD([sQuery(id+"F0.wireOp",EDGE,"E100"),sQuery(id+"F0.wireOp",EDGE,"E101")])]});
            var Q55;
            Q55=makeQuery(id+"F3.opExtrude","SWEPT_EDGE",EDGE,{"disambiguationData":[OSD([sQuery(id+"F0.wireOp",EDGE,"E101"),sQuery(id+"F0.wireOp",EDGE,"E102")])]});
            fillet(context, id + "F4", {"entities" : qUnion([Q0, Q1, Q2, Q3, Q4, Q5, Q6, Q7, Q8, Q9, Q10, Q11, Q12, Q13, Q14, Q15, Q16, Q17, Q18, Q19, Q20, Q21, Q22, Q23, Q24, Q25, Q26, Q27, Q28, Q29, Q30, Q31, Q32, Q33, Q34, Q35, Q36, Q37, Q38, Q39, Q40, Q41, Q42, Q43, Q44, Q45, Q46, Q47, Q48, Q49, Q50, Q51, Q52, Q53, Q54, Q55]), "radius" : 1 * mm, "tangentPropagation" : true, "allowEdgeOverflow" : false});
        }
        {
            var Q0;
            Q0=makeQuery(id+"F0.imprint","IMPRINT",FACE,{"disambiguationData":[TD([[makeQuery(id+"F0.imprint","IMPRINT",EDGE,{"derivedFrom":sQuery(id+"F0.wireOp",EDGE,"E79.bottom")}),-1.0]])]});
            var Q1;
            Q1=makeQuery(id+"F0.imprint","IMPRINT",FACE,{"disambiguationData":[TD([[makeQuery(id+"F0.imprint","IMPRINT",EDGE,{"derivedFrom":sQuery(id+"F0.wireOp",EDGE,"E69.bottom")}),1.0]])]});
            var Q2;
            Q2=makeQuery(id+"F0.imprint","IMPRINT",FACE,{"disambiguationData":[TD([[makeQuery(id+"F0.imprint","IMPRINT",EDGE,{"derivedFrom":sQuery(id+"F0.wireOp",EDGE,"E67.bottom")}),1.0]])]});
            var Q3;
            Q3=makeQuery(id+"F0.imprint","IMPRINT",FACE,{"disambiguationData":[TD([[makeQuery(id+"F0.imprint","IMPRINT",EDGE,{"derivedFrom":sQuery(id+"F0.wireOp",EDGE,"CUijvJ4K-8BJc-PUUR-davF-ycTUrIESOPlg.bottom")}),-1.0]])]});
            var Q4;
            Q4=makeQuery(id+"F0.imprint","IMPRINT",FACE,{"disambiguationData":[TD([[makeQuery(id+"F0.imprint","IMPRINT",EDGE,{"derivedFrom":sQuery(id+"F0.wireOp",EDGE,"E70.MirrorCS")}),-1.0]])]});
            var Q5;
            Q5=makeQuery(id+"F0.imprint","IMPRINT",FACE,{"disambiguationData":[TD([[makeQuery(id+"F0.imprint","IMPRINT",EDGE,{"derivedFrom":sQuery(id+"F0.wireOp",EDGE,"E74.MirrorCS")}),-1.0]])]});
            var Q6;
            Q6=makeQuery(id+"F0.imprint","IMPRINT",FACE,{"disambiguationData":[TD([[makeQuery(id+"F0.imprint","IMPRINT",EDGE,{"derivedFrom":sQuery(id+"F0.wireOp",EDGE,"E80.MirrorCS")}),1.0]])]});
            extrude(context, id + "F5", {"entities" : qUnion([Q0, Q1, Q2, Q3, Q4, Q5, Q6]), "operationType" : NewBodyOperationType.ADD, "depth" : 5 * mm, "offsetDistance" : 25 * mm});
        }
        {
            var Q0;
            Q0=makeQuery(id+"F3.opExtrude","SWEPT_EDGE",EDGE,{"disambiguationData":[OSD([sQuery(id+"F0.wireOp",EDGE,"E2"),sQuery(id+"F0.wireOp",EDGE,"E99")])]});
            var Q1;
            Q1=makeQuery(id+"F3.opExtrude","SWEPT_EDGE",EDGE,{"disambiguationData":[OSD([sQuery(id+"F0.wireOp",EDGE,"E2"),sQuery(id+"F0.wireOp",EDGE,"E102")])]});
            fillet(context, id + "F6", {"entities" : qUnion([Q0, Q1]), "radius" : 2 * mm, "tangentPropagation" : true, "allowEdgeOverflow" : false});
        }
        {
            var Q0;
            {var subQ0=sQuery(id+"F0.wireOp",EDGE,"E83.MirrorCS");var subQ1=sQuery(id+"F0.wireOp",EDGE,"E82.MirrorCS");var subQ2=sQuery(id+"F0.wireOp",EDGE,"E81.MirrorCS");var subQ3=sQuery(id+"F0.wireOp",EDGE,"E80.MirrorCS");var subQ4=sQuery(id+"F0.wireOp",EDGE,"E79.right");var subQ5=sQuery(id+"F0.wireOp",EDGE,"E79.left");var subQ6=sQuery(id+"F0.wireOp",EDGE,"E79.top");var subQ7=sQuery(id+"F0.wireOp",EDGE,"E79.bottom");var subQ8=sQuery(id+"F0.wireOp",EDGE,"E77.MirrorCS");var subQ9=sQuery(id+"F0.wireOp",EDGE,"E76.MirrorCS");var subQ10=sQuery(id+"F0.wireOp",EDGE,"E75.MirrorCS");var subQ11=sQuery(id+"F0.wireOp",EDGE,"E74.MirrorCS");var subQ12=sQuery(id+"F0.wireOp",EDGE,"E73.MirrorCS");var subQ13=sQuery(id+"F0.wireOp",EDGE,"E72.MirrorCS");var subQ14=sQuery(id+"F0.wireOp",EDGE,"E71.MirrorCS");var subQ15=sQuery(id+"F0.wireOp",EDGE,"E70.MirrorCS");var subQ16=sQuery(id+"F0.wireOp",EDGE,"E69.right");var subQ17=sQuery(id+"F0.wireOp",EDGE,"E69.left");var subQ18=sQuery(id+"F0.wireOp",EDGE,"E69.top");var subQ19=sQuery(id+"F0.wireOp",EDGE,"E69.bottom");var subQ20=sQuery(id+"F0.wireOp",EDGE,"E67.right");var subQ21=sQuery(id+"F0.wireOp",EDGE,"E67.left");var subQ22=sQuery(id+"F0.wireOp",EDGE,"E67.top");var subQ23=sQuery(id+"F0.wireOp",EDGE,"E67.bottom");Q0=makeQuery(id+"F5.boolean.opBoolean","MERGE",FACE,{"derivedFrom":[makeQuery(id+"F3.opExtrude","CAP_FACE",FACE,{"disambiguationData":[OSD([sQuery(id+"F0.wireOp",EDGE,"E2"),sQuery(id+"F0.wireOp",EDGE,"E4.top"),sQuery(id+"F0.wireOp",EDGE,"E4.left"),sQuery(id+"F0.wireOp",EDGE,"E4.right"),sQuery(id+"F0.wireOp",EDGE,"E6"),sQuery(id+"F0.wireOp",EDGE,"E8"),sQuery(id+"F0.wireOp",EDGE,"E10"),sQuery(id+"F0.wireOp",EDGE,"E11"),sQuery(id+"F0.wireOp",EDGE,"E14.MirrorC"),sQuery(id+"F0.wireOp",EDGE,"E15.MirrorC"),sQuery(id+"F0.wireOp",EDGE,"E16.MirrorC"),sQuery(id+"F0.wireOp",EDGE,"E17.MirrorC"),sQuery(id+"F0.wireOp",EDGE,"E18.bottom"),sQuery(id+"F0.wireOp",EDGE,"E18.top"),sQuery(id+"F0.wireOp",EDGE,"E18.left"),sQuery(id+"F0.wireOp",EDGE,"E18.right"),sQuery(id+"F0.wireOp",EDGE,"E19.bottom"),sQuery(id+"F0.wireOp",EDGE,"E19.left"),sQuery(id+"F0.wireOp",EDGE,"E19.right"),sQuery(id+"F0.wireOp",EDGE,"E20.MirrorCS"),sQuery(id+"F0.wireOp",EDGE,"E21.MirrorCS"),sQuery(id+"F0.wireOp",EDGE,"E22.MirrorCS"),sQuery(id+"F0.wireOp",EDGE,"E23.MirrorCS"),sQuery(id+"F0.wireOp",EDGE,"E24.MirrorCS"),sQuery(id+"F0.wireOp",EDGE,"E25.MirrorCS"),sQuery(id+"F0.wireOp",EDGE,"E27.MirrorCS"),sQuery(id+"F0.wireOp",EDGE,"E1"),subQ23,subQ22,subQ21,subQ20,subQ19,subQ18,subQ17,subQ16,subQ15,subQ14,subQ13,subQ12,subQ11,subQ10,subQ9,subQ8,subQ7,subQ6,subQ5,subQ4,subQ3,subQ2,subQ1,subQ0,sQuery(id+"F0.wireOp",EDGE,"E85.1"),sQuery(id+"F0.wireOp",EDGE,"E85.2"),sQuery(id+"F0.wireOp",EDGE,"E85.4"),sQuery(id+"F0.wireOp",EDGE,"E85.5"),sQuery(id+"F0.wireOp",EDGE,"E86.MirrorCS"),sQuery(id+"F0.wireOp",EDGE,"E87"),sQuery(id+"F0.wireOp",EDGE,"E88"),sQuery(id+"F0.wireOp",EDGE,"E89"),sQuery(id+"F0.wireOp",EDGE,"E90.MirrorCS"),sQuery(id+"F0.wireOp",EDGE,"E91"),sQuery(id+"F0.wireOp",EDGE,"E92"),sQuery(id+"F0.wireOp",EDGE,"E93"),sQuery(id+"F0.wireOp",EDGE,"E94"),sQuery(id+"F0.wireOp",EDGE,"E95.bottom"),sQuery(id+"F0.wireOp",EDGE,"E95.top"),sQuery(id+"F0.wireOp",EDGE,"E95.left"),sQuery(id+"F0.wireOp",EDGE,"E95.right"),sQuery(id+"F0.wireOp",EDGE,"E97"),sQuery(id+"F0.wireOp",EDGE,"E98.MirrorCS"),sQuery(id+"F0.wireOp",EDGE,"E99"),sQuery(id+"F0.wireOp",EDGE,"E100"),sQuery(id+"F0.wireOp",EDGE,"E101"),sQuery(id+"F0.wireOp",EDGE,"E102"),sQuery(id+"F0.wireOp",EDGE,"E105.MirrorC")])],"isStart":true}),makeQuery(id+"F5.opExtrude","CAP_FACE",FACE,{"disambiguationData":[OSD([subQ23,subQ22,subQ21,subQ20])],"isStart":true}),makeQuery(id+"F5.opExtrude","CAP_FACE",FACE,{"disambiguationData":[OSD([subQ19,subQ18,subQ17,subQ16])],"isStart":true}),makeQuery(id+"F5.opExtrude","CAP_FACE",FACE,{"disambiguationData":[OSD([subQ15,subQ14,subQ13,subQ12])],"isStart":true}),makeQuery(id+"F5.opExtrude","CAP_FACE",FACE,{"disambiguationData":[OSD([subQ11,subQ10,subQ9,subQ8])],"isStart":true}),makeQuery(id+"F5.opExtrude","CAP_FACE",FACE,{"disambiguationData":[OSD([subQ7,subQ6,subQ5,subQ4])],"isStart":true}),makeQuery(id+"F5.opExtrude","CAP_FACE",FACE,{"disambiguationData":[OSD([subQ3,subQ2,subQ1,subQ0])],"isStart":true})]});}
            var sketch = newSketch(context, id + "F7", { "sketchPlane" : qUnion([Q0])});
            skCircle(sketch, "E110", {"center": v(0, 0) * mm, "radius": 70.7 * mm});
            skSolve(sketch);
        }
        {
            var Q0;
            Q0 = qSketchRegion(id + "F7", true);
            extrude(context, id + "F8", {"entities" : qUnion([Q0]), "depth" : 1.5 * mm, "offsetDistance" : 25 * mm});
        }
    });
